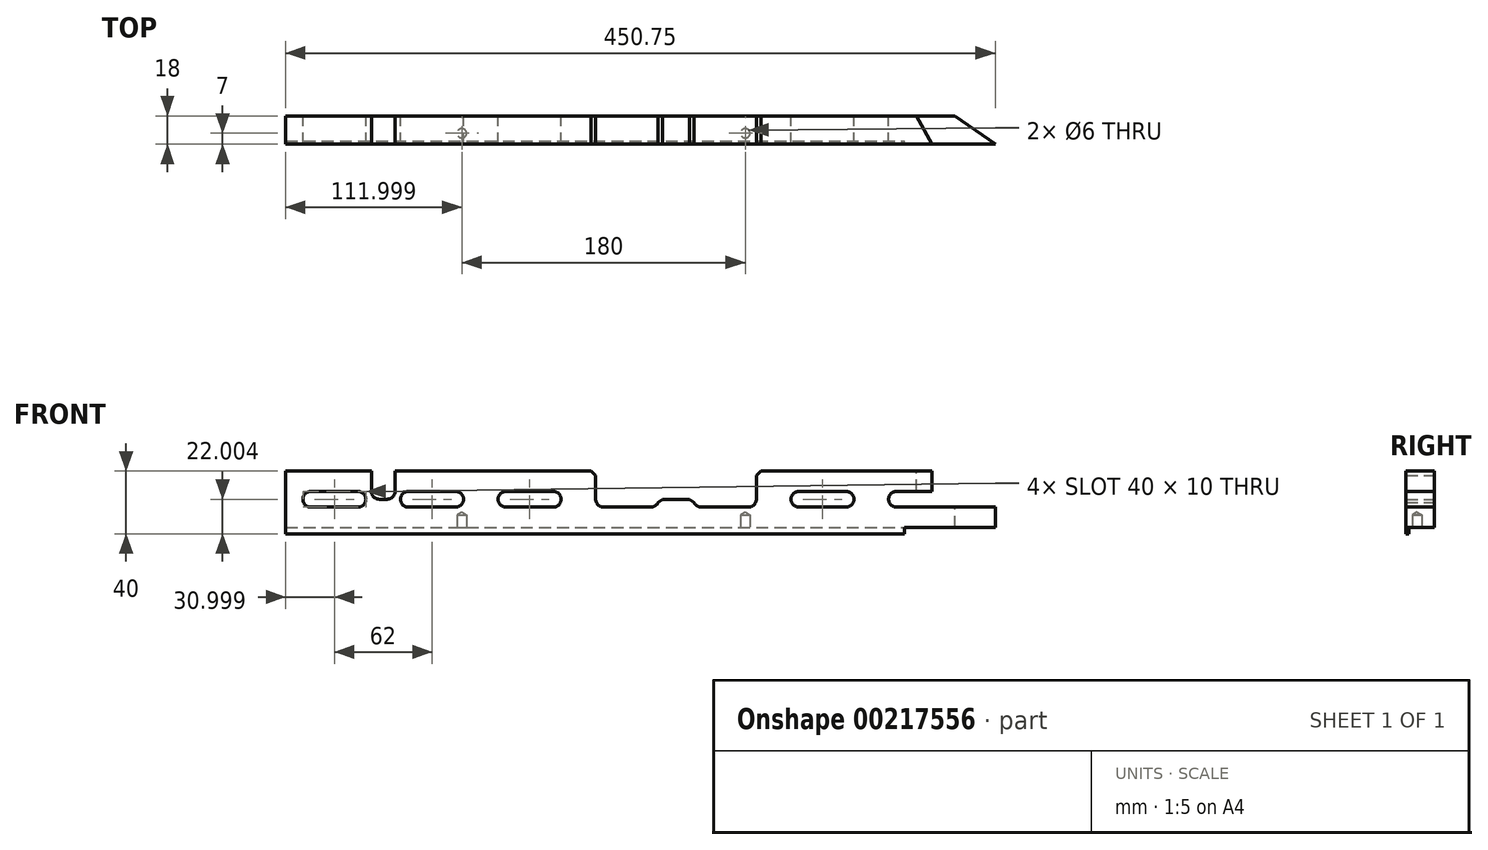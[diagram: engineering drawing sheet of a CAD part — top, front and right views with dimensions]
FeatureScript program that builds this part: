
annotation { "Feature Type Name" : "Feature", "Feature Type Description" : "" }
export const myFeature = defineFeature(function(context is Context, id is Id, definition is map)
    precondition{}
    {
        {
            var Q0;
            Q0=qCreatedBy(makeId("Front.planeOp"),FACE);
            var sketch = newSketch(context, id + "F0", { "sketchPlane" : qUnion([Q0])});
            skLineSegment(sketch, "E0", {"start": v(112.51, 43.03) * mm, "end": v(112.51, 30.03) * mm});
            skLineSegment(sketch, "E1", {"start": v(-282.16, 30.03) * mm, "end": v(-252.16, 30.03) * mm});
            skLineSegment(sketch, "E2", {"start": v(-282.16, 20.03) * mm, "end": v(-252.16, 20.03) * mm});
            skArc(sketch, "E3", {"start": v(-282.16, 30.03) * mm, "mid": v(-287.16, 25.03) * mm, "end": v(-282.16, 20.03) * mm});
            skArc(sketch, "E4", {"start": v(-252.16, 30.03) * mm, "mid": v(-247.16, 25.03) * mm, "end": v(-252.16, 20.03) * mm});
            skLineSegment(sketch, "E5", {"start": v(-220.16, 30.03) * mm, "end": v(-190.16, 30.03) * mm});
            skLineSegment(sketch, "E6", {"start": v(-190.16, 20.03) * mm, "end": v(-220.16, 20.03) * mm});
            skLineSegment(sketch, "E7", {"start": v(-158.16, 30.03) * mm, "end": v(-128.16, 30.03) * mm});
            skLineSegment(sketch, "E8", {"start": v(-128.16, 20.03) * mm, "end": v(-158.16, 20.03) * mm});
            skArc(sketch, "E9", {"start": v(-220.16, 30.03) * mm, "mid": v(-225.16, 25.03) * mm, "end": v(-220.16, 20.03) * mm});
            skArc(sketch, "E10", {"start": v(-190.16, 30.03) * mm, "mid": v(-185.16, 25.03) * mm, "end": v(-190.16, 20.03) * mm});
            skArc(sketch, "E11", {"start": v(-158.16, 30.03) * mm, "mid": v(-163.16, 25.03) * mm, "end": v(-158.16, 20.03) * mm});
            skArc(sketch, "E12", {"start": v(-128.16, 30.03) * mm, "mid": v(-123.16, 25.03) * mm, "end": v(-128.16, 20.03) * mm});
            skLineSegment(sketch, "E13", {"start": v(27.84, 30.03) * mm, "end": v(57.84, 30.03) * mm});
            skLineSegment(sketch, "E14", {"start": v(57.84, 20.03) * mm, "end": v(27.84, 20.03) * mm});
            skArc(sketch, "E15", {"start": v(27.84, 30.03) * mm, "mid": v(22.84, 25.03) * mm, "end": v(27.84, 20.03) * mm});
            skArc(sketch, "E16", {"start": v(57.84, 30.03) * mm, "mid": v(62.84, 25.03) * mm, "end": v(57.84, 20.03) * mm});
            skLineSegment(sketch, "E17", {"start": v(112.51, 30.03) * mm, "end": v(89.84, 30.03) * mm});
            skLineSegment(sketch, "E18", {"start": v(89.84, 20.03) * mm, "end": v(152.6, 20.03) * mm});
            skLineSegment(sketch, "E19", {"start": v(152.6, 20.03) * mm, "end": v(152.6, 7.03) * mm});
            skLineSegment(sketch, "E20", {"start": v(-243.66, 43.03) * mm, "end": v(-243.66, 30.03) * mm});
            skLineSegment(sketch, "E21", {"start": v(-238.66, 25.03) * mm, "end": v(-233.66, 25.03) * mm});
            skLineSegment(sketch, "E22", {"start": v(-228.66, 30.03) * mm, "end": v(-228.66, 43.03) * mm});
            skLineSegment(sketch, "E23", {"start": v(-228.66, 43.03) * mm, "end": v(-104.16, 43.03) * mm});
            skLineSegment(sketch, "E24", {"start": v(-104.16, 43.03) * mm, "end": v(-101.16, 40.03) * mm});
            skLineSegment(sketch, "E25", {"start": v(-101.16, 40.03) * mm, "end": v(-101.16, 25.03) * mm});
            skLineSegment(sketch, "E26", {"start": v(-243.66, 43.03) * mm, "end": v(-298.16, 43.03) * mm});
            skLineSegment(sketch, "E27", {"start": v(-96.16, 20.03) * mm, "end": v(-66.16, 20.03) * mm});
            skLineSegment(sketch, "E28", {"start": v(-61.53, 23.16) * mm, "end": v(-58.74, 25.03) * mm});
            skLineSegment(sketch, "E29", {"start": v(-58.74, 25.03) * mm, "end": v(-41.58, 25.03) * mm});
            skLineSegment(sketch, "E30", {"start": v(-41.58, 25.03) * mm, "end": v(-38.8, 23.16) * mm});
            skLineSegment(sketch, "E31", {"start": v(-34.16, 20.03) * mm, "end": v(-4.16, 20.03) * mm});
            skLineSegment(sketch, "E32", {"start": v(0.84, 25.03) * mm, "end": v(0.84, 40.03) * mm});
            skLineSegment(sketch, "E33", {"start": v(0.84, 40.03) * mm, "end": v(3.84, 43.03) * mm});
            skLineSegment(sketch, "E34", {"start": v(3.84, 43.03) * mm, "end": v(112.51, 43.03) * mm});
            skArc(sketch, "E35", {"start": v(-243.66, 30.03) * mm, "mid": v(-242.2, 26.5) * mm, "end": v(-238.66, 25.03) * mm});
            skArc(sketch, "E36", {"start": v(-233.66, 25.03) * mm, "mid": v(-230.13, 26.5) * mm, "end": v(-228.66, 30.03) * mm});
            skArc(sketch, "E37", {"start": v(-101.16, 25.03) * mm, "mid": v(-99.7, 21.5) * mm, "end": v(-96.16, 20.03) * mm});
            skArc(sketch, "E38", {"start": v(-66.16, 20.03) * mm, "mid": v(-63.37, 20.89) * mm, "end": v(-61.53, 23.16) * mm});
            skArc(sketch, "E39", {"start": v(-34.16, 20.03) * mm, "mid": v(-36.96, 20.89) * mm, "end": v(-38.8, 23.16) * mm});
            skArc(sketch, "E40", {"start": v(-4.16, 20.03) * mm, "mid": v(-0.63, 21.5) * mm, "end": v(0.84, 25.03) * mm});
            skArc(sketch, "E41", {"start": v(89.84, 30.03) * mm, "mid": v(84.84, 25.03) * mm, "end": v(89.84, 20.03) * mm});
            skLineSegment(sketch, "E42", {"start": v(-298.16, 3.03) * mm, "end": v(94.89, 3.03) * mm});
            skLineSegment(sketch, "E43", {"start": v(94.89, 3.03) * mm, "end": v(94.89, 7.03) * mm});
            skLineSegment(sketch, "E44", {"start": v(94.89, 7.03) * mm, "end": v(152.6, 7.03) * mm});
            skLineSegment(sketch, "E45", {"start": v(-298.16, 3.03) * mm, "end": v(-298.16, 43.03) * mm});
            skSolve(sketch);
        }
        {
            var Q0;
            Q0=makeQuery(id+"F0.imprint","IMPRINT",FACE,{"disambiguationData":[TD([[makeQuery(id+"F0.imprint","IMPRINT",EDGE,{"derivedFrom":sQuery(id+"F0.wireOp",EDGE,"E0")}),-1.0]])]});
            extrude(context, id + "F1", {"entities" : qUnion([Q0]), "depth" : 18 * mm});
        }
        {
            var Q0;
            Q0=makeQuery(id+"F1.opExtrude","SWEPT_FACE",FACE,{"disambiguationData":[OSD([sQuery(id+"F0.wireOp",EDGE,"E18")])]});
            var sketch = newSketch(context, id + "F2", { "sketchPlane" : qUnion([Q0])});
            skLineSegment(sketch, "E46", {"start": v(152.6, 0) * mm, "end": v(126.89, 0) * mm});
            skLineSegment(sketch, "E47", {"start": v(126.89, 0) * mm, "end": v(152.6, -18) * mm});
            skLineSegment(sketch, "E48", {"start": v(152.6, -18) * mm, "end": v(152.6, 0) * mm});
            skSolve(sketch);
        }
        {
            var Q0;
            Q0=makeQuery(id+"F2.imprint","IMPRINT",FACE,{"disambiguationData":[TD([[makeQuery(id+"F2.imprint","IMPRINT",EDGE,{"derivedFrom":sQuery(id+"F2.wireOp",EDGE,"E46")}),-1.0]])]});
            extrude(context, id + "F3", {"entities" : qUnion([Q0]), "operationType" : NewBodyOperationType.REMOVE, "oppositeDirection" : true, "depth" : 25 * mm});
        }
        {
            var Q0;
            Q0=makeQuery(id+"F1.opExtrude","SWEPT_FACE",FACE,{"disambiguationData":[OSD([sQuery(id+"F0.wireOp",EDGE,"E34")])]});
            var sketch = newSketch(context, id + "F4", { "sketchPlane" : qUnion([Q0])});
            skLineSegment(sketch, "E49", {"start": v(112.51, 0) * mm, "end": v(102.44, 0) * mm});
            skLineSegment(sketch, "E50", {"start": v(102.44, 0) * mm, "end": v(112.51, -18) * mm});
            skLineSegment(sketch, "E51", {"start": v(112.51, -18) * mm, "end": v(112.51, 0) * mm});
            skSolve(sketch);
        }
        {
            var Q0;
            Q0 = qSketchRegion(id + "F4", true);
            extrude(context, id + "F5", {"entities" : qUnion([Q0]), "operationType" : NewBodyOperationType.REMOVE, "oppositeDirection" : true, "depth" : 18 * mm});
        }
        {
            var Q0;
            Q0=makeQuery(id+"F1.opExtrude","SWEPT_FACE",FACE,{"disambiguationData":[OSD([sQuery(id+"F0.wireOp",EDGE,"E43")])]});
            var sketch = newSketch(context, id + "F6", { "sketchPlane" : qUnion([Q0])});
            skLineSegment(sketch, "E52", {"start": v(-16, 3.03) * mm, "end": v(-16, 7.03) * mm});
            skLineSegment(sketch, "E53", {"start": v(-16, 7.03) * mm, "end": v(0, 7.03) * mm});
            skLineSegment(sketch, "E54", {"start": v(0, 7.03) * mm, "end": v(0, 3.03) * mm});
            skLineSegment(sketch, "E55", {"start": v(0, 3.03) * mm, "end": v(-16, 3.03) * mm});
            skSolve(sketch);
        }
        {
            var Q0;
            Q0=makeQuery(id+"F6.imprint","IMPRINT",FACE,{"disambiguationData":[TD([[makeQuery(id+"F6.imprint","IMPRINT",EDGE,{"derivedFrom":sQuery(id+"F6.wireOp",EDGE,"E52")}),-1.0]])]});
            extrude(context, id + "F7", {"entities" : qUnion([Q0]), "operationType" : NewBodyOperationType.REMOVE, "oppositeDirection" : true, "depth" : 600 * mm});
        }
        {
            var Q0;
            Q0=makeQuery(id+"F7.boolean.opBoolean","MERGE",FACE,{"derivedFrom":[makeQuery(id+"F1.opExtrude","SWEPT_FACE",FACE,{"disambiguationData":[OSD([sQuery(id+"F0.wireOp",EDGE,"E44")])]}),makeQuery(id+"F7.opExtrude","SWEPT_FACE",FACE,{"disambiguationData":[OSD([sQuery(id+"F6.wireOp",EDGE,"E53")])]})]});
            var sketch = newSketch(context, id + "F8", { "sketchPlane" : qUnion([Q0])});
            skCircle(sketch, "E56", {"center": v(-6.16, 11) * mm, "radius": 3 * mm});
            skCircle(sketch, "E57", {"center": v(-186.16, 11) * mm, "radius": 3 * mm});
            skSolve(sketch);
        }
        {
            var Q0;
            Q0=sQuery(id+"F8.wireOp",VERTEX,"E57.center");
            var Q1;
            Q1=sQuery(id+"F8.wireOp",VERTEX,"E56.center");
            var Q2;
            Q2=makeQuery(id+"F1.opExtrude","SWEPT_BODY",BODY,{"disambiguationData":[OSD([sQuery(id+"F0.wireOp",EDGE,"E0"),sQuery(id+"F0.wireOp",EDGE,"E1"),sQuery(id+"F0.wireOp",EDGE,"E2"),sQuery(id+"F0.wireOp",EDGE,"E3"),sQuery(id+"F0.wireOp",EDGE,"E4"),sQuery(id+"F0.wireOp",EDGE,"E5"),sQuery(id+"F0.wireOp",EDGE,"E6"),sQuery(id+"F0.wireOp",EDGE,"E7"),sQuery(id+"F0.wireOp",EDGE,"E8"),sQuery(id+"F0.wireOp",EDGE,"E9"),sQuery(id+"F0.wireOp",EDGE,"E10"),sQuery(id+"F0.wireOp",EDGE,"E11"),sQuery(id+"F0.wireOp",EDGE,"E12"),sQuery(id+"F0.wireOp",EDGE,"E13"),sQuery(id+"F0.wireOp",EDGE,"E14"),sQuery(id+"F0.wireOp",EDGE,"E15"),sQuery(id+"F0.wireOp",EDGE,"E16"),sQuery(id+"F0.wireOp",EDGE,"E17"),sQuery(id+"F0.wireOp",EDGE,"E18"),sQuery(id+"F0.wireOp",EDGE,"E19"),sQuery(id+"F0.wireOp",EDGE,"E20"),sQuery(id+"F0.wireOp",EDGE,"E21"),sQuery(id+"F0.wireOp",EDGE,"E22"),sQuery(id+"F0.wireOp",EDGE,"E23"),sQuery(id+"F0.wireOp",EDGE,"E24"),sQuery(id+"F0.wireOp",EDGE,"E25"),sQuery(id+"F0.wireOp",EDGE,"E26"),sQuery(id+"F0.wireOp",EDGE,"E27"),sQuery(id+"F0.wireOp",EDGE,"E28"),sQuery(id+"F0.wireOp",EDGE,"E29"),sQuery(id+"F0.wireOp",EDGE,"E30"),sQuery(id+"F0.wireOp",EDGE,"E31"),sQuery(id+"F0.wireOp",EDGE,"E32"),sQuery(id+"F0.wireOp",EDGE,"E33"),sQuery(id+"F0.wireOp",EDGE,"E34"),sQuery(id+"F0.wireOp",EDGE,"E35"),sQuery(id+"F0.wireOp",EDGE,"E36"),sQuery(id+"F0.wireOp",EDGE,"E37"),sQuery(id+"F0.wireOp",EDGE,"E38"),sQuery(id+"F0.wireOp",EDGE,"E39"),sQuery(id+"F0.wireOp",EDGE,"E40"),sQuery(id+"F0.wireOp",EDGE,"E41"),sQuery(id+"F0.wireOp",EDGE,"E42"),sQuery(id+"F0.wireOp",EDGE,"E43"),sQuery(id+"F0.wireOp",EDGE,"E44"),sQuery(id+"F0.wireOp",EDGE,"E45")])]});
            hole(context, id + "F9", {"style" : HoleStyle.SIMPLE, "endStyle" : HoleEndStyle.BLIND, "standardTappedOrClearance" : lookupTablePath({ "standard" : "ISO", "size" : "6", "type" : "Drilled" }), "standardBlindInLast" : lookupTablePath({ "standard" : "ISO", "size" : "6", "type" : "Drilled" }), "holeDiameter" : 6 * mm, "holeDepth" : 8 * mm, "startFromSketch" : true, "locations" : qUnion([Q0, Q1]), "scope" : qUnion([Q2])});
        }
    });
